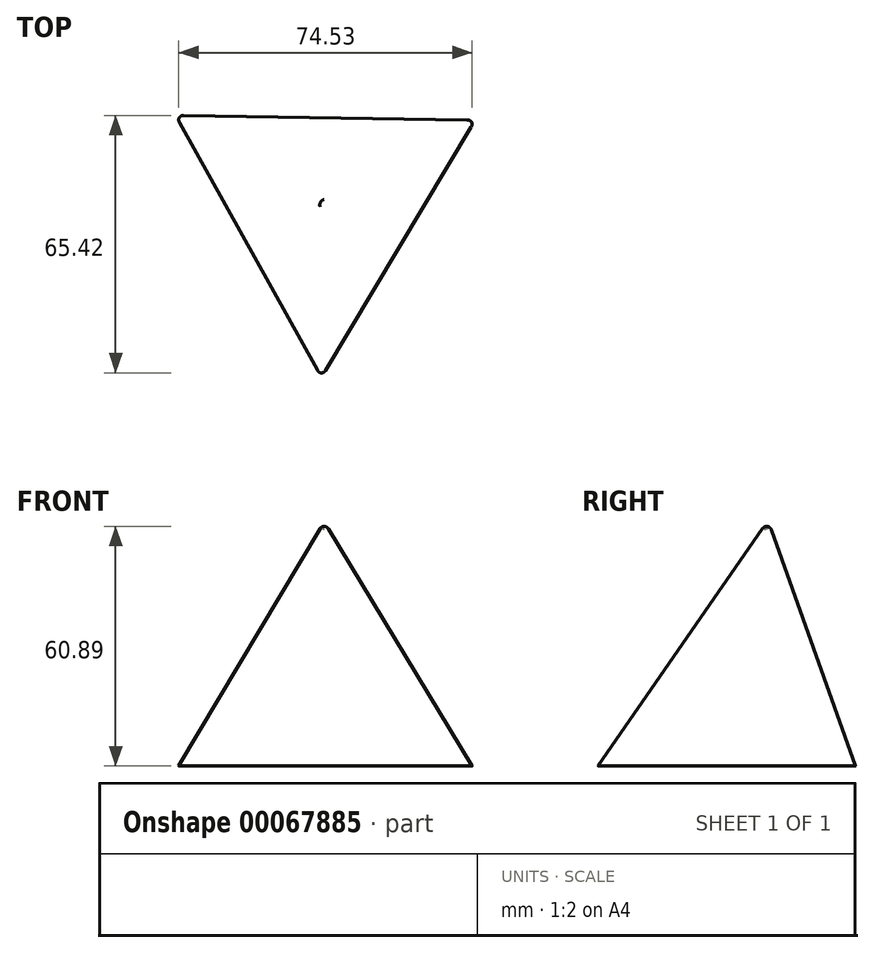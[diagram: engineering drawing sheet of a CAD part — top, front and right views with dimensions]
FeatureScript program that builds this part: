
annotation { "Feature Type Name" : "Feature", "Feature Type Description" : "" }
export const myFeature = defineFeature(function(context is Context, id is Id, definition is map)
    precondition{}
    {
        {
            var Q0;
            Q0=qCreatedBy(makeId("Top.planeOp"),FACE);
            var sketch = newSketch(context, id + "F0", { "sketchPlane" : qUnion([Q0])});
            skCircle(sketch, "E0.cCircle", {"center": v(0, 0) * mm, "radius": 22 * mm, "construction": true});
            skLineSegment(sketch, "E0.0", {"start": v(-0.7, -43.99) * mm, "end": v(-37.75, 22.6) * mm});
            skLineSegment(sketch, "E0.1", {"start": v(-37.75, 22.6) * mm, "end": v(38.44, 21.4) * mm});
            skLineSegment(sketch, "E0.2", {"start": v(38.44, 21.4) * mm, "end": v(-0.7, -43.99) * mm});
            skPoint(sketch, "E0.0.midPoint", {"position": v(-19.22, -10.7) * mm});
            skSolve(sketch);
        }
        {
            var Q0;
            Q0=makeQuery(id+"F0.imprint","IMPRINT",FACE,{"disambiguationData":[TD([[makeQuery(id+"F0.imprint","IMPRINT",EDGE,{"derivedFrom":sQuery(id+"F0.wireOp",EDGE,"E0.0")}),-1.0]])]});
            extrude(context, id + "F1", {"entities" : qUnion([Q0]), "depth" : 0.03 * mm});
        }
        {
            var Q0;
            Q0=qCreatedBy(makeId("Top.planeOp"),FACE);
            cPlane(context, id + "F2", {"entities" : qUnion([Q0]), "cplaneType" : CPlaneType.OFFSET, "offset" : 63.5 * mm, "width" : 152.4 * mm, "height" : 152.4 * mm});
        }
        {
            var Q0;
            Q0=qCreatedBy(id+"F2.planeOp",FACE);
            var sketch = newSketch(context, id + "F3", { "sketchPlane" : qUnion([Q0])});
            skPoint(sketch, "E1", {"position": v(0, 0) * mm});
            skSolve(sketch);
        }
        {
            var Q1;
            Q1=makeQuery(id+"F1.opExtrude","CAP_FACE",FACE,{"disambiguationData":[OSD([sQuery(id+"F0.wireOp",EDGE,"E0.0"),sQuery(id+"F0.wireOp",EDGE,"E0.1"),sQuery(id+"F0.wireOp",EDGE,"E0.2")])],"isStart":false});
            var Q2;
            Q2=sQuery(id+"F3.wireOp",VERTEX,"E1");
            loft(context, id + "F4", {"operationType" : NewBodyOperationType.ADD, "sheetProfilesArray" : [{ "sheetProfileEntities" : qUnion([Q1]) }, { "sheetProfileEntities" : qUnion([Q2]) }]});
        }
        {
            var Q0;
            Q0=makeQuery(id+"F4.opLoft","SWEPT_EDGE",EDGE,{"disambiguationData":[OSD([sQuery(id+"F0.wireOp",EDGE,"E0.0"),sQuery(id+"F0.wireOp",EDGE,"E0.1"),sQuery(id+"F3.wireOp",VERTEX,"E1")])]});
            var Q1;
            Q1=makeQuery(id+"F1.opExtrude","CAP_EDGE",EDGE,{"disambiguationData":[OSD([sQuery(id+"F0.wireOp",EDGE,"E0.0")])],"isStart":true});
            var Q2;
            Q2=makeQuery(id+"F1.opExtrude","CAP_EDGE",EDGE,{"disambiguationData":[OSD([sQuery(id+"F0.wireOp",EDGE,"E0.2")])],"isStart":true});
            var Q3;
            Q3=makeQuery(id+"F1.opExtrude","CAP_EDGE",EDGE,{"disambiguationData":[OSD([sQuery(id+"F0.wireOp",EDGE,"E0.1")])],"isStart":true});
            var Q4;
            Q4=makeQuery(id+"F4.opLoft","SWEPT_EDGE",EDGE,{"disambiguationData":[OSD([sQuery(id+"F0.wireOp",EDGE,"E0.1"),sQuery(id+"F0.wireOp",EDGE,"E0.2"),sQuery(id+"F3.wireOp",VERTEX,"E1")])]});
            var Q5;
            Q5=makeQuery(id+"F4.opLoft","SWEPT_EDGE",EDGE,{"disambiguationData":[OSD([sQuery(id+"F0.wireOp",EDGE,"E0.0"),sQuery(id+"F0.wireOp",EDGE,"E0.2"),sQuery(id+"F3.wireOp",VERTEX,"E1")])]});
            fillet(context, id + "F5", {"entities" : qUnion([Q0, Q1, Q2, Q3, Q4, Q5]), "radius" : 1.27 * mm, "allowEdgeOverflow" : false});
        }
    });
